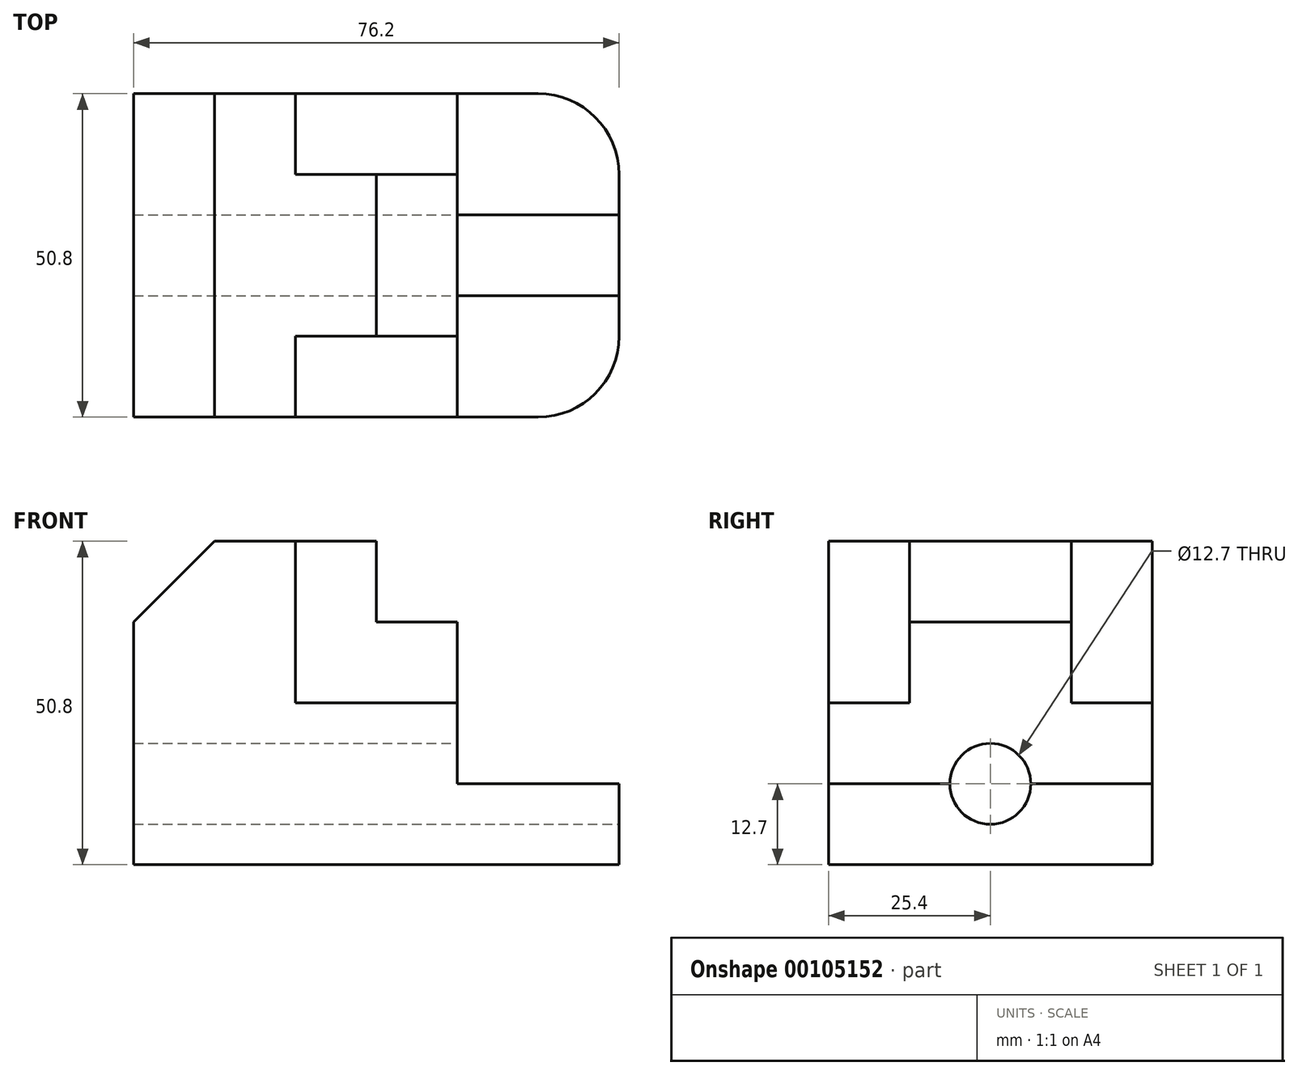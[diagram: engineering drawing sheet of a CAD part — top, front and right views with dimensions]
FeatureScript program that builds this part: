
annotation { "Feature Type Name" : "Feature", "Feature Type Description" : "" }
export const myFeature = defineFeature(function(context is Context, id is Id, definition is map)
    precondition{}
    {
        {
            var Q0;
            Q0=qCreatedBy(makeId("Front.planeOp"),FACE);
            var sketch = newSketch(context, id + "F0", { "sketchPlane" : qUnion([Q0])});
            skLineSegment(sketch, "E0", {"start": v(0, 0) * mm, "end": v(0, 38.1) * mm});
            skLineSegment(sketch, "E1", {"start": v(0, 38.1) * mm, "end": v(12.7, 50.8) * mm});
            skLineSegment(sketch, "E2", {"start": v(12.7, 50.8) * mm, "end": v(38.1, 50.8) * mm});
            skLineSegment(sketch, "E3", {"start": v(38.1, 50.8) * mm, "end": v(38.1, 38.1) * mm});
            skLineSegment(sketch, "E4", {"start": v(38.1, 38.1) * mm, "end": v(50.8, 38.1) * mm});
            skLineSegment(sketch, "E5", {"start": v(50.8, 38.1) * mm, "end": v(50.8, 12.7) * mm});
            skLineSegment(sketch, "E6", {"start": v(50.8, 12.7) * mm, "end": v(76.2, 12.7) * mm});
            skLineSegment(sketch, "E7", {"start": v(76.2, 12.7) * mm, "end": v(76.2, 0) * mm});
            skLineSegment(sketch, "E8", {"start": v(76.2, 0) * mm, "end": v(0, 0) * mm});
            skSolve(sketch);
        }
        {
            var Q0;
            Q0 = qSketchRegion(id + "F0", true);
            extrude(context, id + "F1", {"entities" : qUnion([Q0]), "depth" : 50.8 * mm});
        }
        {
            var Q0;
            Q0=makeQuery(id+"F1.opExtrude","SWEPT_FACE",FACE,{"disambiguationData":[OSD([sQuery(id+"F0.wireOp",EDGE,"E2")])]});
            var sketch = newSketch(context, id + "F2", { "sketchPlane" : qUnion([Q0])});
            skLineSegment(sketch, "E9.bottom", {"start": v(25.4, -50.8) * mm, "end": v(50.8, -50.8) * mm});
            skLineSegment(sketch, "E9.top", {"start": v(25.4, -38.1) * mm, "end": v(50.8, -38.1) * mm});
            skLineSegment(sketch, "E9.left", {"start": v(25.4, -50.8) * mm, "end": v(25.4, -38.1) * mm});
            skLineSegment(sketch, "E9.right", {"start": v(50.8, -50.8) * mm, "end": v(50.8, -38.1) * mm});
            skLineSegment(sketch, "E10.bottom", {"start": v(25.4, 0) * mm, "end": v(50.8, 0) * mm});
            skLineSegment(sketch, "E10.top", {"start": v(25.4, -12.7) * mm, "end": v(50.8, -12.7) * mm});
            skLineSegment(sketch, "E10.left", {"start": v(25.4, 0) * mm, "end": v(25.4, -12.7) * mm});
            skLineSegment(sketch, "E10.right", {"start": v(50.8, 0) * mm, "end": v(50.8, -12.7) * mm});
            skSolve(sketch);
        }
        {
            var Q0;
            Q0 = qSketchRegion(id + "F2", true);
            extrude(context, id + "F3", {"entities" : qUnion([Q0]), "operationType" : NewBodyOperationType.REMOVE, "oppositeDirection" : true, "depth" : 25.4 * mm});
        }
        {
            var Q0;
            Q0=makeQuery(id+"F1.opExtrude","SWEPT_FACE",FACE,{"disambiguationData":[OSD([sQuery(id+"F0.wireOp",EDGE,"E6")])]});
            var sketch = newSketch(context, id + "F4", { "sketchPlane" : qUnion([Q0])});
            skLineSegment(sketch, "E11", {"start": v(63.5, 0) * mm, "end": v(63.5, -50.8) * mm, "construction": true});
            skLineSegment(sketch, "E12", {"start": v(63.5, -38.1) * mm, "end": v(76.2, -38.1) * mm, "construction": true});
            skLineSegment(sketch, "E13", {"start": v(63.5, -12.7) * mm, "end": v(76.2, -12.7) * mm, "construction": true});
            skArc(sketch, "E14", {"start": v(76.2, -12.7) * mm, "mid": v(72.48, -3.72) * mm, "end": v(63.5, 0) * mm});
            skArc(sketch, "E15", {"start": v(63.5, -50.8) * mm, "mid": v(72.48, -47.08) * mm, "end": v(76.2, -38.1) * mm});
            skLineSegment(sketch, "E16", {"start": v(63.5, 0) * mm, "end": v(76.2, 0) * mm});
            skLineSegment(sketch, "E17", {"start": v(76.2, 0) * mm, "end": v(76.2, -12.7) * mm});
            skLineSegment(sketch, "E18", {"start": v(63.5, -50.8) * mm, "end": v(76.2, -50.8) * mm});
            skLineSegment(sketch, "E19", {"start": v(76.2, -50.8) * mm, "end": v(76.2, -38.1) * mm});
            skSolve(sketch);
        }
        {
            var Q0;
            Q0 = qSketchRegion(id + "F4", true);
            extrude(context, id + "F5", {"entities" : qUnion([Q0]), "operationType" : NewBodyOperationType.REMOVE, "endBound" : BoundingType.THROUGH_ALL, "oppositeDirection" : true, "depth" : 25.4 * mm});
        }
        {
            var Q0;
            Q0=makeQuery(id+"F1.opExtrude","SWEPT_FACE",FACE,{"disambiguationData":[OSD([sQuery(id+"F0.wireOp",EDGE,"E7")])]});
            var sketch = newSketch(context, id + "F6", { "sketchPlane" : qUnion([Q0])});
            skCircle(sketch, "E20", {"center": v(-25.4, 12.7) * mm, "radius": 6.35 * mm});
            skSolve(sketch);
        }
        {
            var Q0;
            Q0 = qSketchRegion(id + "F6", true);
            extrude(context, id + "F7", {"entities" : qUnion([Q0]), "operationType" : NewBodyOperationType.REMOVE, "endBound" : BoundingType.THROUGH_ALL, "oppositeDirection" : true, "depth" : 25.4 * mm});
        }
    });
